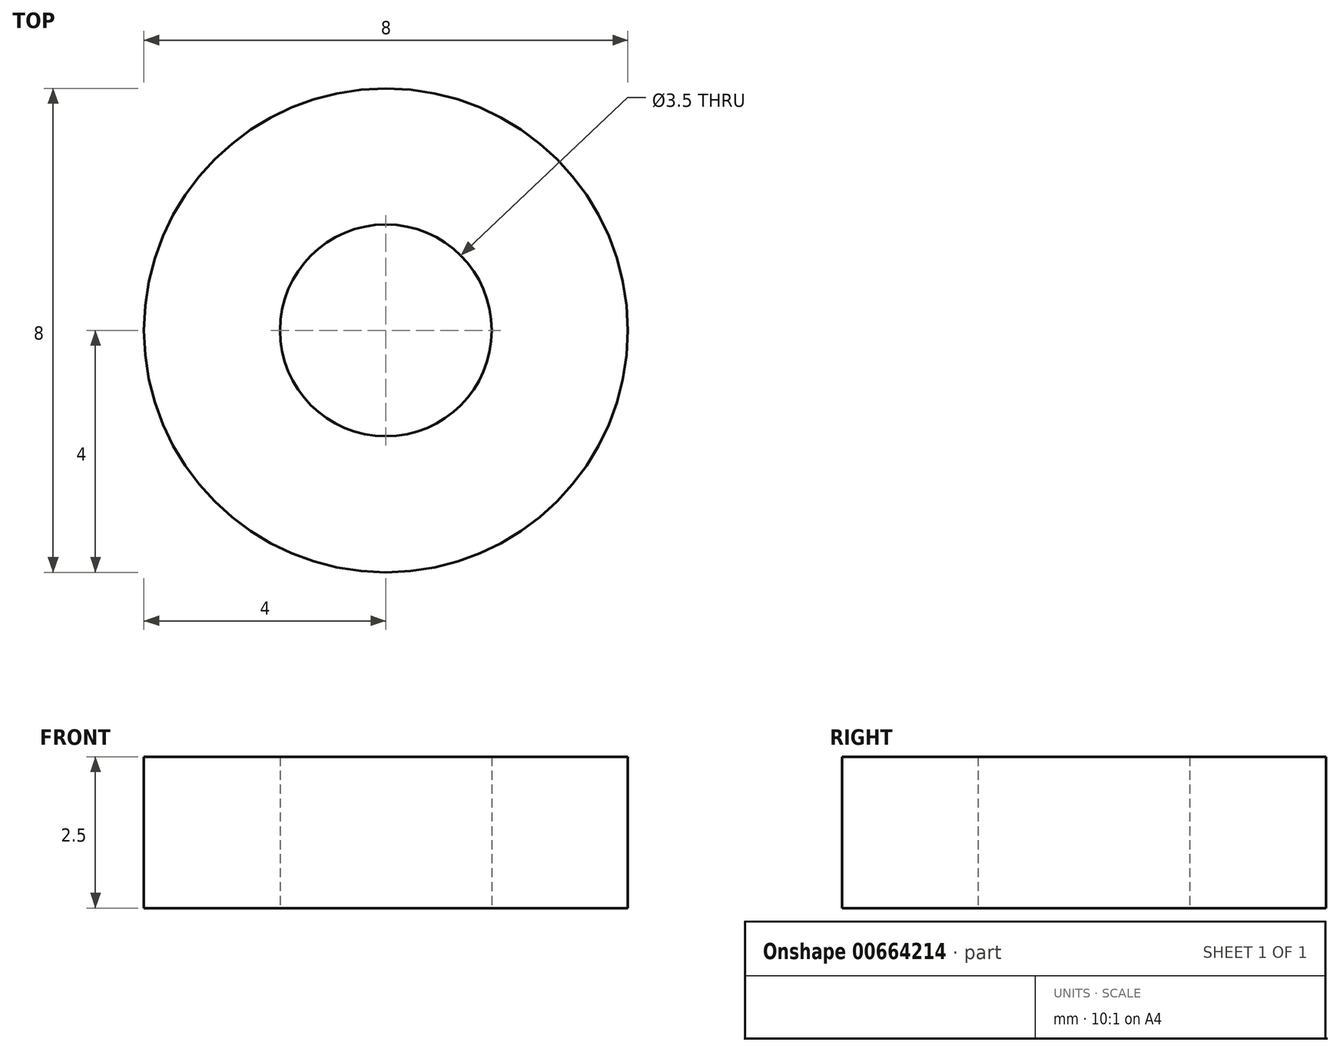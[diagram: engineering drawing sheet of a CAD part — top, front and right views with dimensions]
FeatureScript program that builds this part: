
annotation { "Feature Type Name" : "Feature", "Feature Type Description" : "" }
export const myFeature = defineFeature(function(context is Context, id is Id, definition is map)
    precondition{}
    {
        {
            var Q0;
            Q0=qCreatedBy(makeId("Top.planeOp"),FACE);
            var sketch = newSketch(context, id + "F0", { "sketchPlane" : qUnion([Q0])});
            skCircle(sketch, "E0", {"center": v(0, 0) * mm, "radius": 1.75 * mm});
            skCircle(sketch, "E1", {"center": v(0, 0) * mm, "radius": 4 * mm});
            skSolve(sketch);
        }
        {
            var Q0;
            Q0=makeQuery(id+"F0.imprint","IMPRINT",FACE,{"disambiguationData":[TD([[makeQuery(id+"F0.imprint","IMPRINT",EDGE,{"derivedFrom":sQuery(id+"F0.wireOp",EDGE,"E0")}),-1.0]])]});
            extrude(context, id + "F1", {"entities" : qUnion([Q0]), "depth" : 2.5 * mm, "offsetDistance" : 25 * mm});
        }
    });
